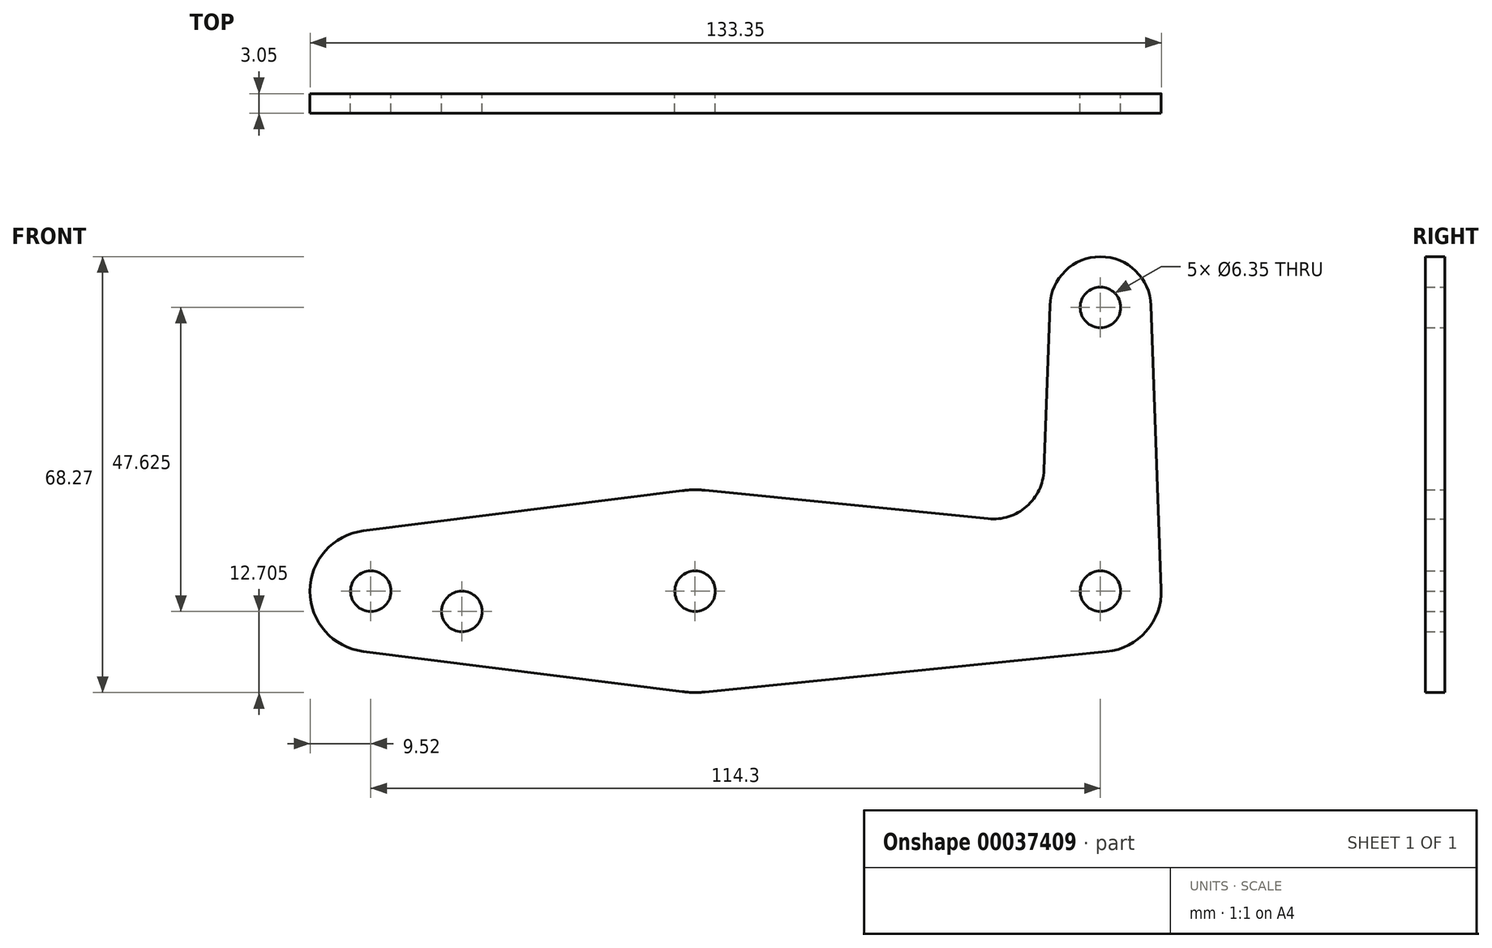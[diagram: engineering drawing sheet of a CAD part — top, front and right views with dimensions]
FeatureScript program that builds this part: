
annotation { "Feature Type Name" : "Feature", "Feature Type Description" : "" }
export const myFeature = defineFeature(function(context is Context, id is Id, definition is map)
    precondition{}
    {
        {
            var Q0;
            Q0=qCreatedBy(makeId("Front.planeOp"),FACE);
            var sketch = newSketch(context, id + "F0", { "sketchPlane" : qUnion([Q0])});
            skCircle(sketch, "E0", {"center": v(-50.8, 0) * mm, "radius": 9.53 * mm});
            skCircle(sketch, "E1", {"center": v(63.5, 0) * mm, "radius": 9.53 * mm});
            skCircle(sketch, "E2", {"center": v(63.5, 0) * mm, "radius": 3.18 * mm});
            skCircle(sketch, "E3", {"center": v(-50.8, 0) * mm, "radius": 3.18 * mm});
            skCircle(sketch, "E4", {"center": v(0, 0) * mm, "radius": 15.88 * mm});
            skLineSegment(sketch, "E5", {"start": v(-52, 9.45) * mm, "end": v(-1.98, 15.75) * mm});
            skLineSegment(sketch, "E6", {"start": v(1.59, 15.8) * mm, "end": v(45.9, 11.34) * mm});
            skLineSegment(sketch, "E7", {"start": v(1.59, -15.8) * mm, "end": v(64.45, -9.48) * mm});
            skLineSegment(sketch, "E8", {"start": v(-52, -9.45) * mm, "end": v(-1.98, -15.75) * mm});
            skCircle(sketch, "E9", {"center": v(-36.53, -3.18) * mm, "radius": 3.18 * mm});
            skCircle(sketch, "E10", {"center": v(0, 0) * mm, "radius": 3.18 * mm});
            skCircle(sketch, "E11", {"center": v(63.5, 44.45) * mm, "radius": 7.94 * mm});
            skLineSegment(sketch, "E12", {"start": v(71.43, 44.73) * mm, "end": v(73.02, 0.34) * mm});
            skLineSegment(sketch, "E13", {"start": v(55.57, 44.73) * mm, "end": v(54.65, 18.97) * mm});
            skArc(sketch, "E14.filletArc", {"start": v(45.9, 11.34) * mm, "mid": v(51.93, 13.26) * mm, "end": v(54.65, 18.97) * mm});
            skCircle(sketch, "E15", {"center": v(63.5, 44.45) * mm, "radius": 3.18 * mm});
            skSolve(sketch);
        }
        {
            var Q0;
            Q0 = qSketchRegion(id + "F0", true);
            extrude(context, id + "F1", {"entities" : qUnion([Q0]), "depth" : 3.05 * mm});
        }
    });
